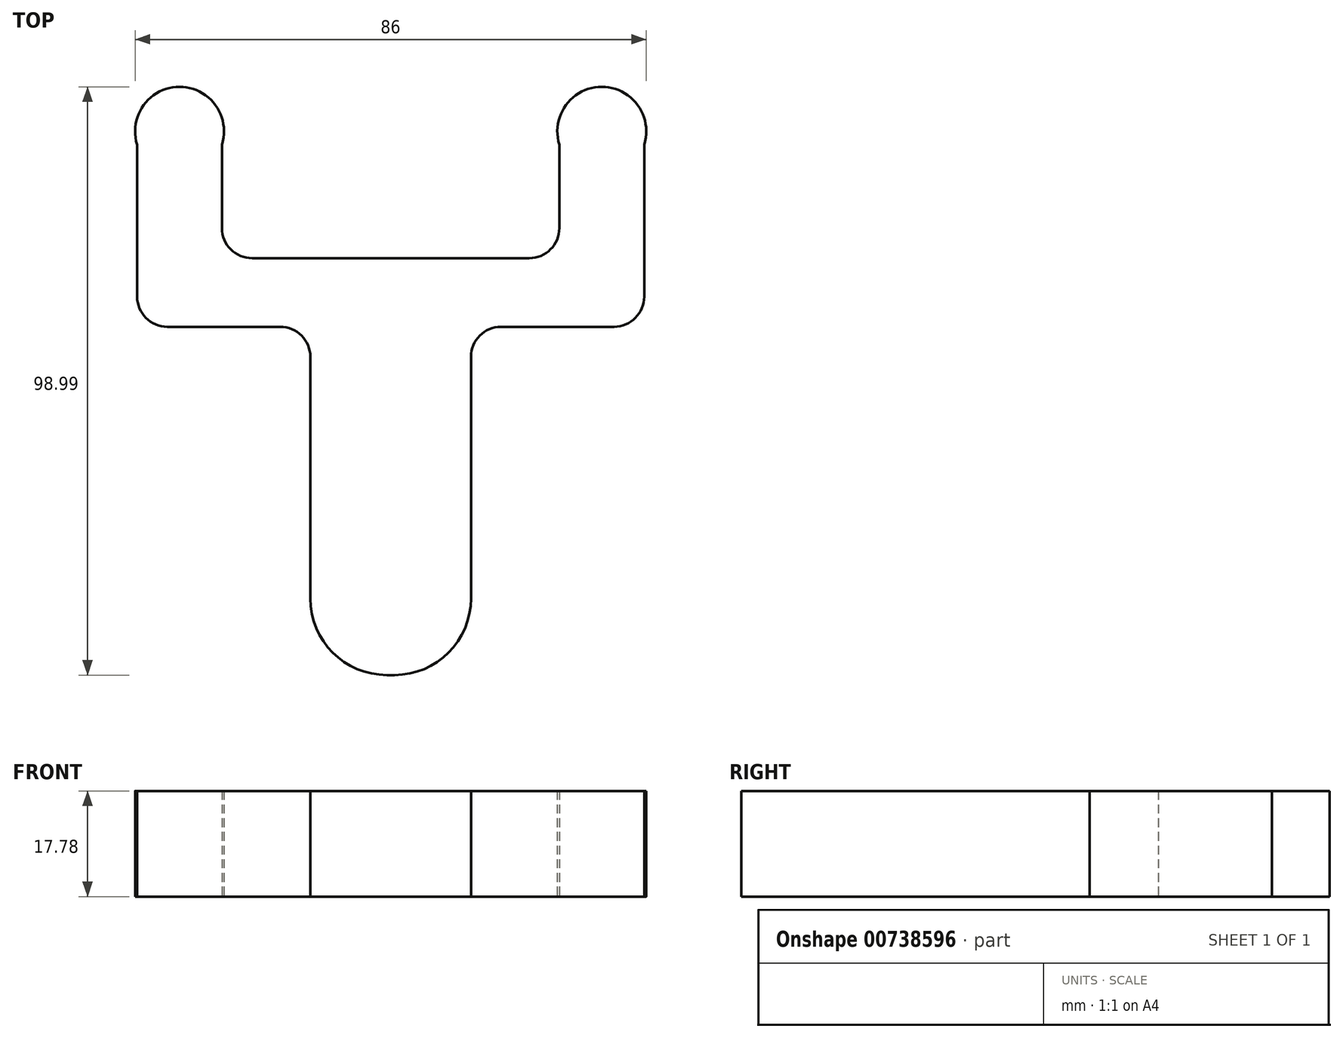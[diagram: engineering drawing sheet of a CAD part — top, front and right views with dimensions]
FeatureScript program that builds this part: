
annotation { "Feature Type Name" : "Feature", "Feature Type Description" : "" }
export const myFeature = defineFeature(function(context is Context, id is Id, definition is map)
    precondition{}
    {
        {
            var Q0;
            Q0=qCreatedBy(makeId("Top.planeOp"),FACE);
            var sketch = newSketch(context, id + "F0", { "sketchPlane" : qUnion([Q0])});
            skPoint(sketch, "E0.start.orphan", {"position": v(0, -44.94) * mm});
            skLineSegment(sketch, "E1", {"start": v(0, -44.94) * mm, "end": v(-13.51, -44.94) * mm});
            skLineSegment(sketch, "E2", {"start": v(-13.51, -44.94) * mm, "end": v(-13.51, 13.66) * mm});
            skLineSegment(sketch, "E3", {"start": v(-13.51, 13.66) * mm, "end": v(-42.66, 13.66) * mm});
            skLineSegment(sketch, "E4", {"start": v(-42.66, 13.66) * mm, "end": v(-42.66, 44.33) * mm});
            skLineSegment(sketch, "E5", {"start": v(-28.4, 44.33) * mm, "end": v(-28.4, 25.2) * mm});
            skLineSegment(sketch, "E6", {"start": v(-28.4, 25.2) * mm, "end": v(0, 25.2) * mm});
            skLineSegment(sketch, "E7.MirrorCS", {"start": v(28.4, 25.2) * mm, "end": v(0, 25.2) * mm});
            skLineSegment(sketch, "E8.MirrorCS", {"start": v(13.51, 13.66) * mm, "end": v(42.66, 13.66) * mm});
            skLineSegment(sketch, "E9.MirrorCS", {"start": v(28.4, 44.33) * mm, "end": v(28.4, 25.2) * mm});
            skLineSegment(sketch, "E10.MirrorCS", {"start": v(42.66, 13.66) * mm, "end": v(42.66, 44.33) * mm});
            skLineSegment(sketch, "E11.MirrorCS", {"start": v(13.51, -44.94) * mm, "end": v(13.51, 13.66) * mm});
            skLineSegment(sketch, "E12.MirrorCS", {"start": v(0, -44.94) * mm, "end": v(13.51, -44.94) * mm});
            skArc(sketch, "E13", {"start": v(-28.4, 44.33) * mm, "mid": v(-35.53, 54.05) * mm, "end": v(-42.66, 44.33) * mm});
            skPoint(sketch, "E13.second.point", {"position": v(-35.53, 54.05) * mm});
            skPoint(sketch, "E13.second.point.positionSnap0", {"position": v(-35.53, 44.33) * mm});
            skArc(sketch, "E14.MirrorCS", {"start": v(28.4, 44.33) * mm, "mid": v(35.53, 54.05) * mm, "end": v(42.66, 44.33) * mm});
            skPoint(sketch, "E15.MirrorCS.end.orphan", {"position": v(28.4, 44.33) * mm});
            skPoint(sketch, "E15.MirrorCS.start.orphan", {"position": v(42.66, 44.33) * mm});
            skSolve(sketch);
        }
        {
            var Q0;
            Q0 = qSketchRegion(id + "F0", true);
            extrude(context, id + "F1", {"entities" : qUnion([Q0]), "depth" : 17.78 * mm, "offsetDistance" : 25.4 * mm});
        }
        {
            var Q0;
            Q0=makeQuery(id+"F1.opExtrude","SWEPT_EDGE",EDGE,{"disambiguationData":[OSD([sQuery(id+"F0.wireOp",EDGE,"E3"),sQuery(id+"F0.wireOp",EDGE,"E4")])]});
            var Q1;
            Q1=makeQuery(id+"F1.opExtrude","SWEPT_EDGE",EDGE,{"disambiguationData":[OSD([sQuery(id+"F0.wireOp",EDGE,"E2"),sQuery(id+"F0.wireOp",EDGE,"E3")])]});
            var Q2;
            Q2=makeQuery(id+"F1.opExtrude","SWEPT_EDGE",EDGE,{"disambiguationData":[OSD([sQuery(id+"F0.wireOp",EDGE,"E8.MirrorCS"),sQuery(id+"F0.wireOp",EDGE,"E10.MirrorCS")])]});
            var Q3;
            Q3=makeQuery(id+"F1.opExtrude","SWEPT_EDGE",EDGE,{"disambiguationData":[OSD([sQuery(id+"F0.wireOp",EDGE,"E8.MirrorCS"),sQuery(id+"F0.wireOp",EDGE,"E11.MirrorCS")])]});
            var Q4;
            Q4=makeQuery(id+"F1.opExtrude","SWEPT_EDGE",EDGE,{"disambiguationData":[OSD([sQuery(id+"F0.wireOp",EDGE,"E7.MirrorCS"),sQuery(id+"F0.wireOp",EDGE,"E9.MirrorCS")])]});
            var Q5;
            Q5=makeQuery(id+"F1.opExtrude","SWEPT_EDGE",EDGE,{"disambiguationData":[OSD([sQuery(id+"F0.wireOp",EDGE,"E5"),sQuery(id+"F0.wireOp",EDGE,"E6")])]});
            fillet(context, id + "F2", {"entities" : qUnion([Q0, Q1, Q2, Q3, Q4, Q5]), "radius" : 5.08 * mm, "tangentPropagation" : true, "allowEdgeOverflow" : false});
        }
        {
            var Q0;
            Q0=makeQuery(id+"F1.opExtrude","SWEPT_EDGE",EDGE,{"disambiguationData":[OSD([sQuery(id+"F0.wireOp",EDGE,"E1"),sQuery(id+"F0.wireOp",EDGE,"E2")])]});
            var Q1;
            Q1=makeQuery(id+"F1.opExtrude","SWEPT_EDGE",EDGE,{"disambiguationData":[OSD([sQuery(id+"F0.wireOp",EDGE,"E11.MirrorCS"),sQuery(id+"F0.wireOp",EDGE,"E12.MirrorCS")])]});
            fillet(context, id + "F3", {"entities" : qUnion([Q0, Q1]), "radius" : 12.88 * mm, "tangentPropagation" : true, "allowEdgeOverflow" : false});
        }
    });
